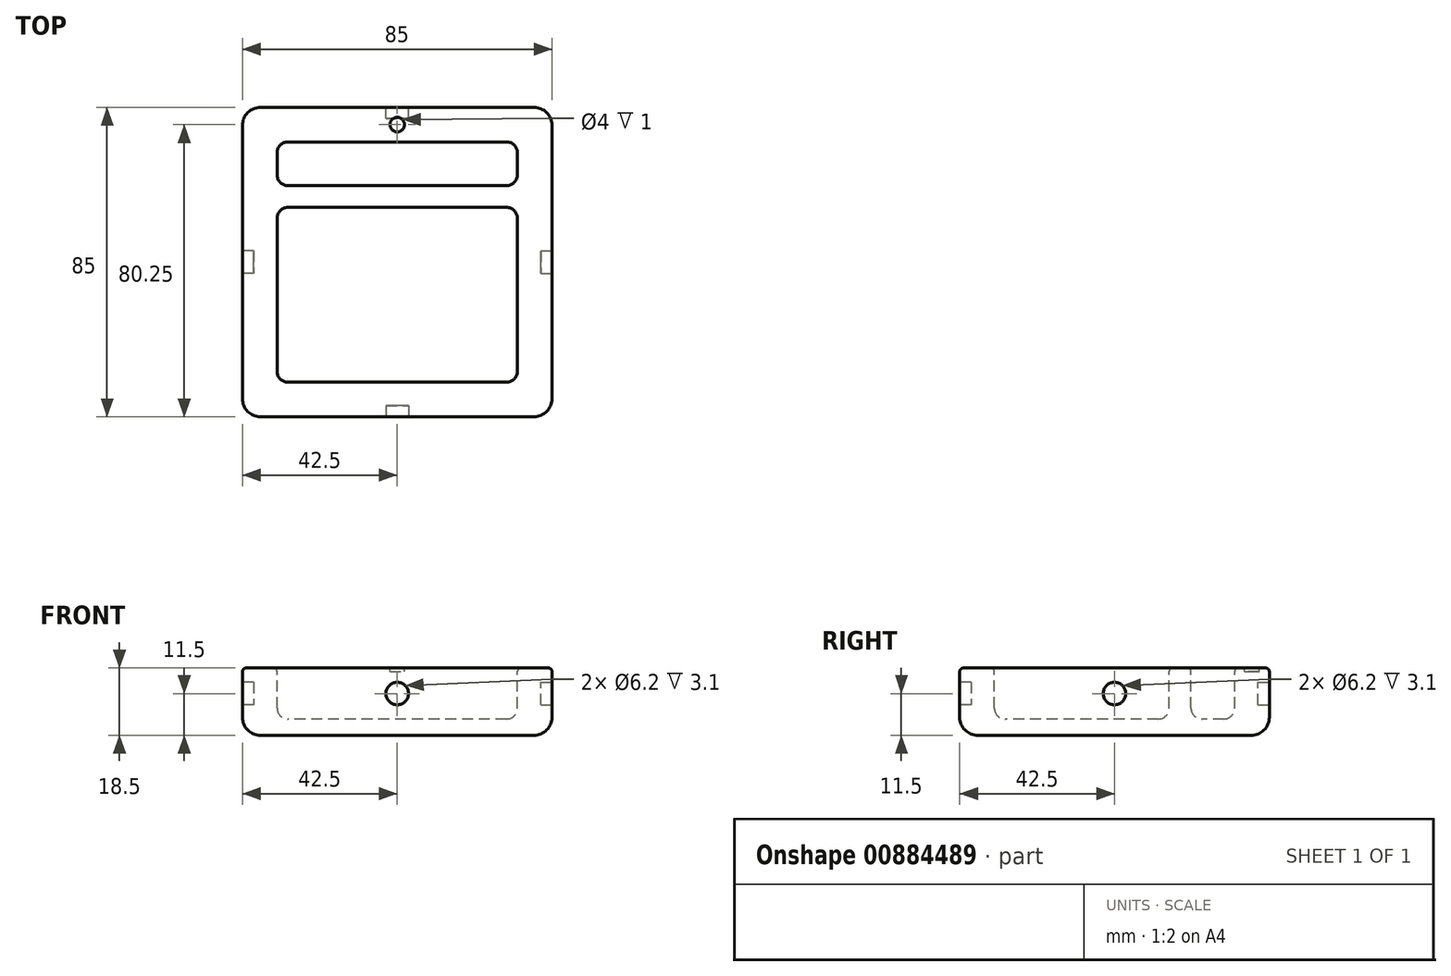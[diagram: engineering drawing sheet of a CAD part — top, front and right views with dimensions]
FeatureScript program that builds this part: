
annotation { "Feature Type Name" : "Feature", "Feature Type Description" : "" }
export const myFeature = defineFeature(function(context is Context, id is Id, definition is map)
    precondition{}
    {
        {
            var Q0;
            Q0=qCreatedBy(makeId("Top.planeOp"),FACE);
            var sketch = newSketch(context, id + "F0", { "sketchPlane" : qUnion([Q0])});
            skLineSegment(sketch, "E0.bottom", {"start": v(-42.5, 42.5) * mm, "end": v(42.5, 42.5) * mm});
            skLineSegment(sketch, "E0.top", {"start": v(-42.5, -42.5) * mm, "end": v(42.5, -42.5) * mm});
            skLineSegment(sketch, "E0.left", {"start": v(-42.5, 42.5) * mm, "end": v(-42.5, -42.5) * mm});
            skLineSegment(sketch, "E0.right", {"start": v(42.5, 42.5) * mm, "end": v(42.5, -42.5) * mm});
            skLineSegment(sketch, "E1.bottom", {"start": v(-30, 33) * mm, "end": v(30, 33) * mm});
            skLineSegment(sketch, "E1.top", {"start": v(-30, 21) * mm, "end": v(30, 21) * mm});
            skLineSegment(sketch, "E1.left", {"start": v(-33, 30) * mm, "end": v(-33, 24) * mm});
            skLineSegment(sketch, "E1.right", {"start": v(33, 30) * mm, "end": v(33, 24) * mm});
            skLineSegment(sketch, "E2.direction1", {"start": v(-33, 21) * mm, "end": v(-8.24, 21) * mm, "construction": true});
            skPoint(sketch, "E3.visualSharp", {"position": v(-33, 33) * mm});
            skArc(sketch, "E3.filletArc", {"start": v(-30, 33) * mm, "mid": v(-32.12, 32.12) * mm, "end": v(-33, 30) * mm});
            skPoint(sketch, "E4.visualSharp", {"position": v(33, 33) * mm});
            skArc(sketch, "E4.filletArc", {"start": v(33, 30) * mm, "mid": v(32.12, 32.12) * mm, "end": v(30, 33) * mm});
            skPoint(sketch, "E5.visualSharp", {"position": v(33, 21) * mm});
            skArc(sketch, "E5.filletArc", {"start": v(30, 21) * mm, "mid": v(32.12, 21.88) * mm, "end": v(33, 24) * mm});
            skPoint(sketch, "E6.visualSharp", {"position": v(-33, 21) * mm});
            skArc(sketch, "E6.filletArc", {"start": v(-33, 24) * mm, "mid": v(-32.12, 21.88) * mm, "end": v(-30, 21) * mm});
            skLineSegment(sketch, "E7.direction1", {"start": v(-33, 21) * mm, "end": v(-6.5, 21) * mm, "construction": true});
            skLineSegment(sketch, "E8", {"start": v(-42.5, 0) * mm, "end": v(42.5, 0) * mm, "construction": true});
            skLineSegment(sketch, "E9", {"start": v(0, -42.5) * mm, "end": v(0, 42.5) * mm, "construction": true});
            skLineSegment(sketch, "E10.bottom", {"start": v(-30, 15) * mm, "end": v(30, 15) * mm});
            skLineSegment(sketch, "E10.top", {"start": v(-30, -33) * mm, "end": v(30, -33) * mm});
            skLineSegment(sketch, "E10.left", {"start": v(-33, 12) * mm, "end": v(-33, -30) * mm});
            skLineSegment(sketch, "E10.right", {"start": v(33, 12) * mm, "end": v(33, -30) * mm});
            skLineSegment(sketch, "E11.direction1", {"start": v(-33, -33) * mm, "end": v(12.67, -33) * mm, "construction": true});
            skPoint(sketch, "E12.visualSharp", {"position": v(-33, 15) * mm});
            skArc(sketch, "E12.filletArc", {"start": v(-30, 15) * mm, "mid": v(-32.12, 14.12) * mm, "end": v(-33, 12) * mm});
            skPoint(sketch, "E13.visualSharp", {"position": v(33, 15) * mm});
            skArc(sketch, "E13.filletArc", {"start": v(33, 12) * mm, "mid": v(32.12, 14.12) * mm, "end": v(30, 15) * mm});
            skPoint(sketch, "E14.visualSharp", {"position": v(33, -33) * mm});
            skArc(sketch, "E14.filletArc", {"start": v(30, -33) * mm, "mid": v(32.12, -32.12) * mm, "end": v(33, -30) * mm});
            skPoint(sketch, "E15.visualSharp", {"position": v(-33, -33) * mm});
            skArc(sketch, "E15.filletArc", {"start": v(-33, -30) * mm, "mid": v(-32.12, -32.12) * mm, "end": v(-30, -33) * mm});
            skLineSegment(sketch, "E16.direction1", {"start": v(-33, -33) * mm, "end": v(14.41, -33) * mm, "construction": true});
            skCircle(sketch, "E17", {"center": v(0, 37.75) * mm, "radius": 2 * mm});
            skSolve(sketch);
        }
        {
            assignVariable(context, id + "F1", {"name" : "h", "anyValue" : 18.5});
        }
        {
            assignVariable(context, id + "F2", {"name" : "d", "anyValue" : 14});
        }
        {
            var Q0;
            Q0=makeQuery(id+"F0.imprint","IMPRINT",FACE,{"disambiguationData":[TD([[makeQuery(id+"F0.imprint","IMPRINT",EDGE,{"derivedFrom":sQuery(id+"F0.wireOp",EDGE,"E1.bottom")}),-1.0]])]});
            var Q1;
            Q1=makeQuery(id+"F0.imprint","IMPRINT",FACE,{"disambiguationData":[TD([[makeQuery(id+"F0.imprint","IMPRINT",EDGE,{"derivedFrom":sQuery(id+"F0.wireOp",EDGE,"E0.bottom")}),-1.0]])]});
            var Q2;
            Q2=makeQuery(id+"F0.imprint","IMPRINT",FACE,{"disambiguationData":[TD([[makeQuery(id+"F0.imprint","IMPRINT",EDGE,{"derivedFrom":sQuery(id+"F0.wireOp",EDGE,"E2.0.2.0")}),1.0]])]});
            var Q3;
            Q3=makeQuery(id+"F0.imprint","IMPRINT",FACE,{"disambiguationData":[TD([[makeQuery(id+"F0.imprint","IMPRINT",EDGE,{"derivedFrom":sQuery(id+"F0.wireOp",EDGE,"E2.0.3.0")}),1.0]])]});
            var Q4;
            Q4=makeQuery(id+"F0.imprint","IMPRINT",FACE,{"disambiguationData":[TD([[makeQuery(id+"F0.imprint","IMPRINT",EDGE,{"derivedFrom":sQuery(id+"F0.wireOp",EDGE,"E2.0.1.0")}),1.0]])]});
            var Q5;
            Q5=makeQuery(id+"F0.imprint","IMPRINT",FACE,{"disambiguationData":[TD([[makeQuery(id+"F0.imprint","IMPRINT",EDGE,{"derivedFrom":sQuery(id+"F0.wireOp",EDGE,"E7.0.1.2")}),1.0]])]});
            var Q6;
            Q6=makeQuery(id+"F0.imprint","IMPRINT",FACE,{"disambiguationData":[TD([[makeQuery(id+"F0.imprint","IMPRINT",EDGE,{"derivedFrom":sQuery(id+"F0.wireOp",EDGE,"E7.0.2.2")}),1.0]])]});
            var Q7;
            Q7=makeQuery(id+"F0.imprint","IMPRINT",FACE,{"disambiguationData":[TD([[makeQuery(id+"F0.imprint","IMPRINT",EDGE,{"derivedFrom":sQuery(id+"F0.wireOp",EDGE,"E7.0.3.2")}),1.0]])]});
            var Q8;
            Q8=makeQuery(id+"F0.imprint","IMPRINT",FACE,{"disambiguationData":[TD([[makeQuery(id+"F0.imprint","IMPRINT",EDGE,{"derivedFrom":sQuery(id+"F0.wireOp",EDGE,"E10.bottom")}),-1.0]])]});
            var Q9;
            Q9=makeQuery(id+"F0.imprint","IMPRINT",FACE,{"disambiguationData":[TD([[makeQuery(id+"F0.imprint","IMPRINT",EDGE,{"derivedFrom":sQuery(id+"F0.wireOp",EDGE,"E17")}),1.0]])]});
            extrude(context, id + "F3", {"entities" : qUnion([Q0, Q1, Q2, Q3, Q4, Q5, Q6, Q7, Q8, Q9]), "depth" : (getVariable(context, 'h')) * mm, "offsetDistance" : 25 * mm});
        }
        {
            var Q0;
            Q0=makeQuery(id+"F0.imprint","IMPRINT",FACE,{"disambiguationData":[TD([[makeQuery(id+"F0.imprint","IMPRINT",EDGE,{"derivedFrom":sQuery(id+"F0.wireOp",EDGE,"E1.bottom")}),-1.0]])]});
            var Q1;
            Q1=makeQuery(id+"F0.imprint","IMPRINT",FACE,{"disambiguationData":[TD([[makeQuery(id+"F0.imprint","IMPRINT",EDGE,{"derivedFrom":sQuery(id+"F0.wireOp",EDGE,"E2.0.1.0")}),1.0]])]});
            var Q2;
            Q2=makeQuery(id+"F0.imprint","IMPRINT",FACE,{"disambiguationData":[TD([[makeQuery(id+"F0.imprint","IMPRINT",EDGE,{"derivedFrom":sQuery(id+"F0.wireOp",EDGE,"E2.0.2.0")}),1.0]])]});
            var Q3;
            Q3=makeQuery(id+"F0.imprint","IMPRINT",FACE,{"disambiguationData":[TD([[makeQuery(id+"F0.imprint","IMPRINT",EDGE,{"derivedFrom":sQuery(id+"F0.wireOp",EDGE,"E2.0.3.0")}),1.0]])]});
            var Q4;
            Q4=makeQuery(id+"F0.imprint","IMPRINT",FACE,{"disambiguationData":[TD([[makeQuery(id+"F0.imprint","IMPRINT",EDGE,{"derivedFrom":sQuery(id+"F0.wireOp",EDGE,"E7.0.1.2")}),1.0]])]});
            var Q5;
            Q5=makeQuery(id+"F0.imprint","IMPRINT",FACE,{"disambiguationData":[TD([[makeQuery(id+"F0.imprint","IMPRINT",EDGE,{"derivedFrom":sQuery(id+"F0.wireOp",EDGE,"E7.0.2.2")}),1.0]])]});
            var Q6;
            Q6=makeQuery(id+"F0.imprint","IMPRINT",FACE,{"disambiguationData":[TD([[makeQuery(id+"F0.imprint","IMPRINT",EDGE,{"derivedFrom":sQuery(id+"F0.wireOp",EDGE,"E7.0.3.2")}),1.0]])]});
            var Q7;
            Q7=makeQuery(id+"F0.imprint","IMPRINT",FACE,{"disambiguationData":[TD([[makeQuery(id+"F0.imprint","IMPRINT",EDGE,{"derivedFrom":sQuery(id+"F0.wireOp",EDGE,"E10.bottom")}),-1.0]])]});
            extrude(context, id + "F4", {"entities" : qUnion([Q0, Q1, Q2, Q3, Q4, Q5, Q6, Q7]), "operationType" : NewBodyOperationType.REMOVE, "depth" : (getVariable(context, 'd')) * mm, "offsetDistance" : 25 * mm});
        }
        {
            var Q0;
            Q0=makeQuery(id+"F3.opExtrude","CAP_FACE",FACE,{"disambiguationData":[OSD([sQuery(id+"F0.wireOp",EDGE,"E0.bottom"),sQuery(id+"F0.wireOp",EDGE,"E0.top"),sQuery(id+"F0.wireOp",EDGE,"E0.left"),sQuery(id+"F0.wireOp",EDGE,"E0.right")])],"isStart":false});
            var Q1;
            Q1=makeQuery(id+"F3.opExtrude","SWEPT_EDGE",EDGE,{"disambiguationData":[OSD([sQuery(id+"F0.wireOp",EDGE,"E0.bottom"),sQuery(id+"F0.wireOp",EDGE,"E0.right")])]});
            var Q2;
            Q2=makeQuery(id+"F3.opExtrude","SWEPT_EDGE",EDGE,{"disambiguationData":[OSD([sQuery(id+"F0.wireOp",EDGE,"E0.bottom"),sQuery(id+"F0.wireOp",EDGE,"E0.left")])]});
            var Q3;
            Q3=makeQuery(id+"F3.opExtrude","SWEPT_EDGE",EDGE,{"disambiguationData":[OSD([sQuery(id+"F0.wireOp",EDGE,"E0.top"),sQuery(id+"F0.wireOp",EDGE,"E0.left")])]});
            var Q4;
            Q4=makeQuery(id+"F3.opExtrude","SWEPT_EDGE",EDGE,{"disambiguationData":[OSD([sQuery(id+"F0.wireOp",EDGE,"E0.top"),sQuery(id+"F0.wireOp",EDGE,"E0.right")])]});
            fillet(context, id + "F5", {"entities" : qUnion([Q0, Q1, Q2, Q3, Q4]), "radius" : 5 * mm, "tangentPropagation" : true, "allowEdgeOverflow" : false});
        }
        {
            var Q0;
            Q0=makeQuery(id+"F4.boolean.opBoolean","COPY",FACE,{"derivedFrom":makeQuery(id+"F4.opExtrude","CAP_FACE",FACE,{"disambiguationData":[OSD([sQuery(id+"F0.wireOp",EDGE,"E1.bottom"),sQuery(id+"F0.wireOp",EDGE,"E1.top"),sQuery(id+"F0.wireOp",EDGE,"E1.left"),sQuery(id+"F0.wireOp",EDGE,"E1.right"),sQuery(id+"F0.wireOp",EDGE,"E3.filletArc"),sQuery(id+"F0.wireOp",EDGE,"E4.filletArc"),sQuery(id+"F0.wireOp",EDGE,"E5.filletArc"),sQuery(id+"F0.wireOp",EDGE,"E6.filletArc")])],"isStart":false})});
            var Q1;
            Q1=makeQuery(id+"F4.boolean.opBoolean","COPY",FACE,{"derivedFrom":makeQuery(id+"F4.opExtrude","CAP_FACE",FACE,{"disambiguationData":[OSD([sQuery(id+"F0.wireOp",EDGE,"E7.0.1.2"),sQuery(id+"F0.wireOp",EDGE,"E7.0.1.4"),sQuery(id+"F0.wireOp",EDGE,"E7.0.1.5"),sQuery(id+"F0.wireOp",EDGE,"E7.0.1.6"),sQuery(id+"F0.wireOp",EDGE,"E7.0.1.7"),sQuery(id+"F0.wireOp",EDGE,"E7.0.1.9"),sQuery(id+"F0.wireOp",EDGE,"E7.0.1.11"),sQuery(id+"F0.wireOp",EDGE,"E7.0.1.12")])],"isStart":false})});
            var Q2;
            Q2=makeQuery(id+"F4.boolean.opBoolean","COPY",FACE,{"derivedFrom":makeQuery(id+"F4.opExtrude","CAP_FACE",FACE,{"disambiguationData":[OSD([sQuery(id+"F0.wireOp",EDGE,"E7.0.2.2"),sQuery(id+"F0.wireOp",EDGE,"E7.0.2.4"),sQuery(id+"F0.wireOp",EDGE,"E7.0.2.5"),sQuery(id+"F0.wireOp",EDGE,"E7.0.2.6"),sQuery(id+"F0.wireOp",EDGE,"E7.0.2.7"),sQuery(id+"F0.wireOp",EDGE,"E7.0.2.9"),sQuery(id+"F0.wireOp",EDGE,"E7.0.2.11"),sQuery(id+"F0.wireOp",EDGE,"E7.0.2.12")])],"isStart":false})});
            var Q3;
            Q3=makeQuery(id+"F4.boolean.opBoolean","COPY",FACE,{"derivedFrom":makeQuery(id+"F4.opExtrude","CAP_FACE",FACE,{"disambiguationData":[OSD([sQuery(id+"F0.wireOp",EDGE,"E7.0.3.2"),sQuery(id+"F0.wireOp",EDGE,"E7.0.3.4"),sQuery(id+"F0.wireOp",EDGE,"E7.0.3.5"),sQuery(id+"F0.wireOp",EDGE,"E7.0.3.6"),sQuery(id+"F0.wireOp",EDGE,"E7.0.3.7"),sQuery(id+"F0.wireOp",EDGE,"E7.0.3.9"),sQuery(id+"F0.wireOp",EDGE,"E7.0.3.11"),sQuery(id+"F0.wireOp",EDGE,"E7.0.3.12")])],"isStart":false})});
            var Q4;
            Q4=makeQuery(id+"F4.boolean.opBoolean","COPY",FACE,{"derivedFrom":makeQuery(id+"F4.opExtrude","CAP_FACE",FACE,{"disambiguationData":[OSD([sQuery(id+"F0.wireOp",EDGE,"E10.bottom"),sQuery(id+"F0.wireOp",EDGE,"E10.top"),sQuery(id+"F0.wireOp",EDGE,"E10.left"),sQuery(id+"F0.wireOp",EDGE,"E10.right"),sQuery(id+"F0.wireOp",EDGE,"E12.filletArc"),sQuery(id+"F0.wireOp",EDGE,"E13.filletArc"),sQuery(id+"F0.wireOp",EDGE,"E14.filletArc"),sQuery(id+"F0.wireOp",EDGE,"E15.filletArc")])],"isStart":false})});
            fillet(context, id + "F6", {"entities" : qUnion([Q0, Q1, Q2, Q3, Q4]), "radius" : 3 * mm, "tangentPropagation" : true, "allowEdgeOverflow" : false});
        }
        {
            var Q0;
            Q0=makeQuery(id+"F3.opExtrude","CAP_FACE",FACE,{"disambiguationData":[OSD([sQuery(id+"F0.wireOp",EDGE,"E0.bottom"),sQuery(id+"F0.wireOp",EDGE,"E0.top"),sQuery(id+"F0.wireOp",EDGE,"E0.left"),sQuery(id+"F0.wireOp",EDGE,"E0.right")])],"isStart":true});
            fillet(context, id + "F7", {"entities" : qUnion([Q0]), "radius" : 1 * mm, "tangentPropagation" : true, "allowEdgeOverflow" : false});
        }
        {
            var Q0;
            Q0=makeQuery(id+"F3.opExtrude","SWEPT_FACE",FACE,{"disambiguationData":[OSD([sQuery(id+"F0.wireOp",EDGE,"E0.top")])]});
            var sketch = newSketch(context, id + "F8", { "sketchPlane" : qUnion([Q0])});
            skCircle(sketch, "E18", {"center": v(0, 7) * mm, "radius": 3.1 * mm});
            skSolve(sketch);
        }
        {
            var Q0;
            Q0=makeQuery(id+"F8.imprint","IMPRINT",FACE,{"disambiguationData":[TD([[makeQuery(id+"F8.imprint","IMPRINT",EDGE,{"derivedFrom":sQuery(id+"F8.wireOp",EDGE,"E18")}),1.0]])]});
            extrude(context, id + "F9", {"entities" : qUnion([Q0]), "operationType" : NewBodyOperationType.REMOVE, "oppositeDirection" : true, "depth" : 3.1 * mm, "offsetDistance" : 25 * mm});
        }
        {
            var Q0;
            Q0=makeQuery(id+"F3.opExtrude","SWEPT_FACE",FACE,{"disambiguationData":[OSD([sQuery(id+"F0.wireOp",EDGE,"E0.bottom")])]});
            var sketch = newSketch(context, id + "F10", { "sketchPlane" : qUnion([Q0])});
            skCircle(sketch, "E19", {"center": v(0, 7) * mm, "radius": 3.1 * mm});
            skSolve(sketch);
        }
        {
            var Q0;
            Q0=makeQuery(id+"F10.imprint","IMPRINT",FACE,{"disambiguationData":[TD([[makeQuery(id+"F10.imprint","IMPRINT",EDGE,{"derivedFrom":sQuery(id+"F10.wireOp",EDGE,"E19")}),1.0]])]});
            extrude(context, id + "F11", {"entities" : qUnion([Q0]), "operationType" : NewBodyOperationType.REMOVE, "oppositeDirection" : true, "depth" : 3.1 * mm, "offsetDistance" : 25 * mm});
        }
        {
            var Q0;
            Q0=makeQuery(id+"F3.opExtrude","SWEPT_FACE",FACE,{"disambiguationData":[OSD([sQuery(id+"F0.wireOp",EDGE,"E0.left")])]});
            var sketch = newSketch(context, id + "F12", { "sketchPlane" : qUnion([Q0])});
            skCircle(sketch, "E20", {"center": v(0, 7) * mm, "radius": 3.1 * mm});
            skSolve(sketch);
        }
        {
            var Q0;
            Q0=makeQuery(id+"F12.imprint","IMPRINT",FACE,{"disambiguationData":[TD([[makeQuery(id+"F12.imprint","IMPRINT",EDGE,{"derivedFrom":sQuery(id+"F12.wireOp",EDGE,"E20")}),1.0]])]});
            extrude(context, id + "F13", {"entities" : qUnion([Q0]), "operationType" : NewBodyOperationType.REMOVE, "oppositeDirection" : true, "depth" : 3.1 * mm, "offsetDistance" : 25 * mm});
        }
        {
            var Q0;
            Q0=makeQuery(id+"F3.opExtrude","SWEPT_FACE",FACE,{"disambiguationData":[OSD([sQuery(id+"F0.wireOp",EDGE,"E0.right")])]});
            var sketch = newSketch(context, id + "F14", { "sketchPlane" : qUnion([Q0])});
            skCircle(sketch, "E21", {"center": v(0, 7) * mm, "radius": 3.1 * mm});
            skSolve(sketch);
        }
        {
            var Q0;
            Q0=makeQuery(id+"F14.imprint","IMPRINT",FACE,{"disambiguationData":[TD([[makeQuery(id+"F14.imprint","IMPRINT",EDGE,{"derivedFrom":sQuery(id+"F14.wireOp",EDGE,"E21")}),1.0]])]});
            extrude(context, id + "F15", {"entities" : qUnion([Q0]), "operationType" : NewBodyOperationType.REMOVE, "oppositeDirection" : true, "depth" : 3.1 * mm, "offsetDistance" : 25 * mm});
        }
        {
            var Q0;
            Q0=makeQuery(id+"F0.imprint","IMPRINT",FACE,{"disambiguationData":[TD([[makeQuery(id+"F0.imprint","IMPRINT",EDGE,{"derivedFrom":sQuery(id+"F0.wireOp",EDGE,"E17")}),1.0]])]});
            extrude(context, id + "F16", {"entities" : qUnion([Q0]), "operationType" : NewBodyOperationType.REMOVE, "depth" : 1 * mm, "offsetDistance" : 25 * mm});
        }
        {
            var Q0;
            Q0=makeQuery(id+"F3.opExtrude","SWEPT_BODY",BODY,{"disambiguationData":[OSD([sQuery(id+"F0.wireOp",EDGE,"E0.bottom"),sQuery(id+"F0.wireOp",EDGE,"E0.top"),sQuery(id+"F0.wireOp",EDGE,"E0.left"),sQuery(id+"F0.wireOp",EDGE,"E0.right")])]});
            var Q1;
            Q1=sQuery(id+"F0.wireOp",EDGE,"E9");
            transform(context, id + "F17", {"entities" : qUnion([Q0]), "transformType" : TransformType.ROTATION, "transformAxis" : qUnion([Q1]), "angle" : 180 * degree, "makeCopy" : false});
        }
    });
